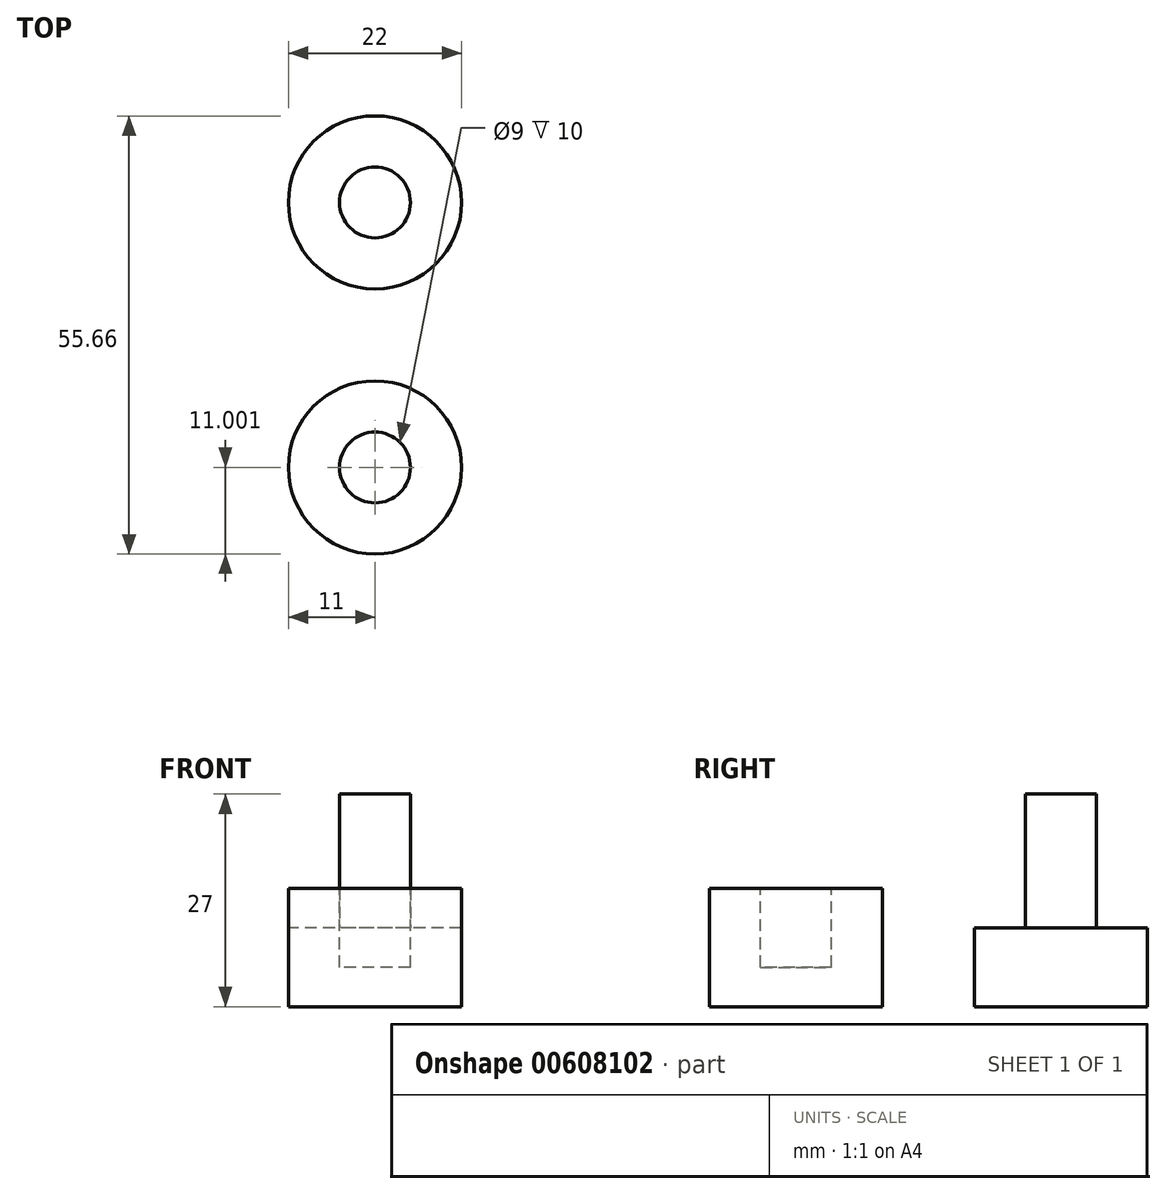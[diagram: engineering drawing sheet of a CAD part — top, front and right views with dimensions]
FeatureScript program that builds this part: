
annotation { "Feature Type Name" : "Feature", "Feature Type Description" : "" }
export const myFeature = defineFeature(function(context is Context, id is Id, definition is map)
    precondition{}
    {
        {
            var Q0;
            Q0=qCreatedBy(makeId("Top.planeOp"),FACE);
            var sketch = newSketch(context, id + "F0", { "sketchPlane" : qUnion([Q0])});
            skCircle(sketch, "E0", {"center": v(0, 0) * mm, "radius": 11 * mm});
            skSolve(sketch);
        }
        {
            var Q0;
            Q0 = qSketchRegion(id + "F0", true);
            extrude(context, id + "F1", {"entities" : qUnion([Q0]), "depth" : 10 * mm, "offsetDistance" : 25 * mm});
        }
        {
            var Q0;
            Q0=makeQuery(id+"F1.opExtrude","CAP_FACE",FACE,{"disambiguationData":[OSD([sQuery(id+"F0.wireOp",EDGE,"E0")])],"isStart":false});
            var sketch = newSketch(context, id + "F2", { "sketchPlane" : qUnion([Q0])});
            skCircle(sketch, "E1", {"center": v(0, 0) * mm, "radius": 4.5 * mm});
            skSolve(sketch);
        }
        {
            var Q0;
            Q0 = qSketchRegion(id + "F2", true);
            extrude(context, id + "F3", {"entities" : qUnion([Q0]), "operationType" : NewBodyOperationType.ADD, "depth" : 17 * mm, "offsetDistance" : 25 * mm});
        }
        {
            var Q0;
            Q0=qCreatedBy(makeId("Top.planeOp"),FACE);
            var sketch = newSketch(context, id + "F4", { "sketchPlane" : qUnion([Q0])});
            skCircle(sketch, "E2", {"center": v(0, -33.66) * mm, "radius": 11 * mm});
            skSolve(sketch);
        }
        {
            var Q0;
            Q0 = qSketchRegion(id + "F4", true);
            extrude(context, id + "F5", {"entities" : qUnion([Q0]), "depth" : 15 * mm, "offsetDistance" : 25 * mm});
        }
        {
            var Q0;
            Q0=makeQuery(id+"F5.opExtrude","CAP_FACE",FACE,{"disambiguationData":[OSD([sQuery(id+"F4.wireOp",EDGE,"E2")])],"isStart":false});
            var sketch = newSketch(context, id + "F6", { "sketchPlane" : qUnion([Q0])});
            skCircle(sketch, "E3", {"center": v(0, -33.66) * mm, "radius": 4.5 * mm});
            skSolve(sketch);
        }
        {
            var Q0;
            Q0 = qSketchRegion(id + "F6", true);
            extrude(context, id + "F7", {"entities" : qUnion([Q0]), "operationType" : NewBodyOperationType.REMOVE, "oppositeDirection" : true, "depth" : 10 * mm, "offsetDistance" : 25 * mm});
        }
    });
